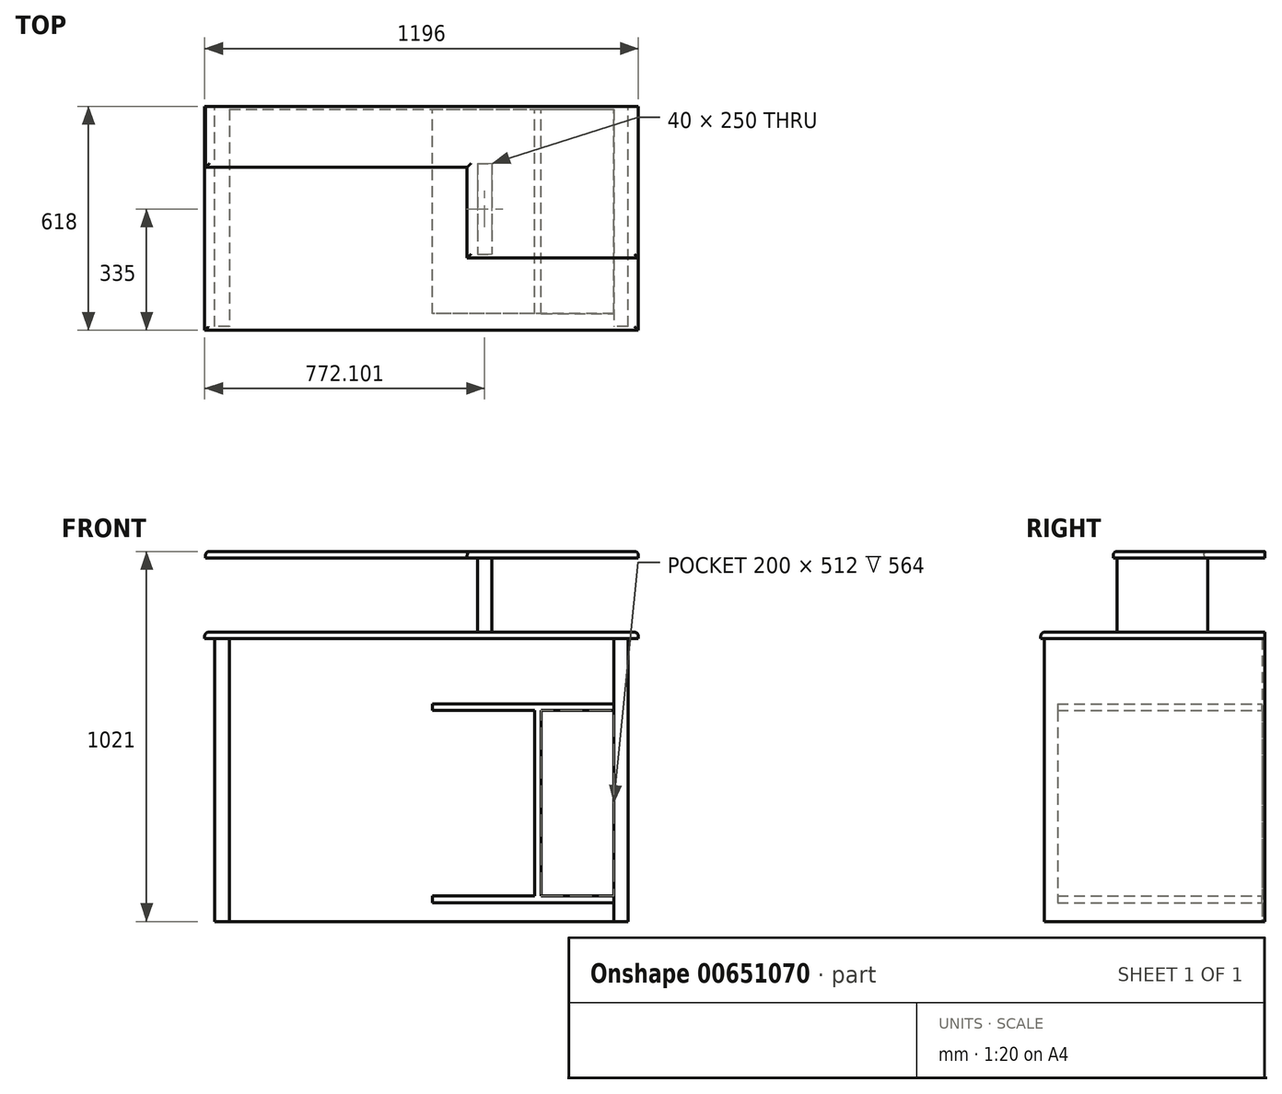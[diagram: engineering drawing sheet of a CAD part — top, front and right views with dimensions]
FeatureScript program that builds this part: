
annotation { "Feature Type Name" : "Feature", "Feature Type Description" : "" }
export const myFeature = defineFeature(function(context is Context, id is Id, definition is map)
    precondition{}
    {
        {
            var Q0;
            Q0=qCreatedBy(makeId("Top.planeOp"),FACE);
            var sketch = newSketch(context, id + "F0", { "sketchPlane" : qUnion([Q0])});
            skLineSegment(sketch, "E0.bottom", {"start": v(0, 0) * mm, "end": v(-1140, 0) * mm});
            skLineSegment(sketch, "E0.top", {"start": v(0, 608) * mm, "end": v(-1140, 608) * mm});
            skLineSegment(sketch, "E0.left", {"start": v(0, 0) * mm, "end": v(0, 608) * mm});
            skLineSegment(sketch, "E0.right", {"start": v(-1140, 0) * mm, "end": v(-1140, 608) * mm});
            skLineSegment(sketch, "E1.bottom", {"start": v(-1100, 600) * mm, "end": v(-40, 600) * mm});
            skLineSegment(sketch, "E1.top", {"start": v(-1100, 0) * mm, "end": v(-40, 0) * mm});
            skLineSegment(sketch, "E1.left", {"start": v(-1100, 600) * mm, "end": v(-1100, 0) * mm});
            skLineSegment(sketch, "E1.right", {"start": v(-40, 600) * mm, "end": v(-40, 0) * mm});
            skLineSegment(sketch, "E2.bottom", {"start": v(-558, 600) * mm, "end": v(-540, 600) * mm});
            skLineSegment(sketch, "E2.top", {"start": v(-558, 36) * mm, "end": v(-540, 36) * mm});
            skLineSegment(sketch, "E2.left", {"start": v(-558, 600) * mm, "end": v(-558, 36) * mm});
            skLineSegment(sketch, "E2.right", {"start": v(-540, 600) * mm, "end": v(-540, 36) * mm});
            skSolve(sketch);
        }
        {
            var Q0;
            Q0=makeQuery(id+"F0.imprint","IMPRINT",FACE,{"disambiguationData":[TD([[makeQuery(id+"F0.imprint","IMPRINT",EDGE,{"derivedFrom":sQuery(id+"F0.wireOp",EDGE,"E0.top")}),1.0]])]});
            var Q1;
            Q1=makeQuery(id+"F0.imprint","IMPRINT",FACE,{"disambiguationData":[TD([[makeQuery(id+"F0.imprint","IMPRINT",EDGE,{"derivedFrom":sQuery(id+"F0.wireOp",EDGE,"E2.bottom")}),-1.0]])]});
            extrude(context, id + "F1", {"entities" : qUnion([Q0, Q1]), "depth" : 780 * mm, "offsetDistance" : 25 * mm});
        }
        {
            var Q0;
            {var subQ0=sQuery(id+"F0.wireOp",EDGE,"E1.bottom");Q0=makeQuery(id+"F1.opExtrude","SWEPT_FACE",FACE,{"disambiguationData":[OSD([subQ0]),TDD([makeQuery(id+"F0.imprint","IMPRINT",EDGE,{"disambiguationData":[TD([[makeQuery(id+"F0.imprint","INTERSECT",VERTEX,{"derivedFrom":[subQ0,sQuery(id+"F0.wireOp",EDGE,"E1.right")]}),1.0]])],"derivedFrom":subQ0})])]});}
            var sketch = newSketch(context, id + "F2", { "sketchPlane" : qUnion([Q0])});
            skLineSegment(sketch, "E3.bottom", {"start": v(-540, 52) * mm, "end": v(-40, 52) * mm});
            skLineSegment(sketch, "E3.top", {"start": v(-540, 70) * mm, "end": v(-40, 70) * mm});
            skLineSegment(sketch, "E3.left", {"start": v(-540, 52) * mm, "end": v(-540, 70) * mm});
            skLineSegment(sketch, "E3.right", {"start": v(-40, 52) * mm, "end": v(-40, 70) * mm});
            skLineSegment(sketch, "E4.bottom", {"start": v(-40, 582) * mm, "end": v(-540, 582) * mm});
            skLineSegment(sketch, "E4.top", {"start": v(-40, 600) * mm, "end": v(-540, 600) * mm});
            skLineSegment(sketch, "E4.left", {"start": v(-40, 582) * mm, "end": v(-40, 600) * mm});
            skLineSegment(sketch, "E4.right", {"start": v(-540, 582) * mm, "end": v(-540, 600) * mm});
            skLineSegment(sketch, "E5.0", {"start": v(-1100, 780) * mm, "end": v(-558, 780) * mm});
            skLineSegment(sketch, "E6.bottom", {"start": v(-258, 582) * mm, "end": v(-240, 582) * mm});
            skLineSegment(sketch, "E6.top", {"start": v(-258, 70) * mm, "end": v(-240, 70) * mm});
            skLineSegment(sketch, "E6.left", {"start": v(-258, 582) * mm, "end": v(-258, 70) * mm});
            skLineSegment(sketch, "E6.right", {"start": v(-240, 582) * mm, "end": v(-240, 70) * mm});
            skSolve(sketch);
        }
        {
            var Q0;
            Q0=qSketchRegion(id+"F2",true);
            extrude(context, id + "F3", {"entities" : qUnion([Q0]), "operationType" : NewBodyOperationType.ADD, "depth" : 564 * mm, "offsetDistance" : 25 * mm});
        }
        {
            var Q0;
            Q0=makeQuery(id+"F1.opExtrude","CAP_FACE",FACE,{"disambiguationData":[OSD([sQuery(id+"F0.wireOp",EDGE,"E0.bottom"),sQuery(id+"F0.wireOp",EDGE,"E0.top"),sQuery(id+"F0.wireOp",EDGE,"E0.left"),sQuery(id+"F0.wireOp",EDGE,"E0.right"),sQuery(id+"F0.wireOp",EDGE,"E1.bottom"),sQuery(id+"F0.wireOp",EDGE,"E1.left"),sQuery(id+"F0.wireOp",EDGE,"E1.right"),sQuery(id+"F0.wireOp",EDGE,"E2.top"),sQuery(id+"F0.wireOp",EDGE,"E2.left"),sQuery(id+"F0.wireOp",EDGE,"E2.right")])],"isStart":false});
            var sketch = newSketch(context, id + "F4", { "sketchPlane" : qUnion([Q0])});
            skLineSegment(sketch, "E7.0", {"start": v(0, 608) * mm, "end": v(-1140, 608) * mm});
            skLineSegment(sketch, "E8.0", {"start": v(-1140, 0) * mm, "end": v(-1140, 608) * mm});
            skLineSegment(sketch, "E9.0", {"start": v(0, 0) * mm, "end": v(0, 608) * mm});
            skLineSegment(sketch, "E10.0", {"start": v(-1100, 0) * mm, "end": v(-1140, 0) * mm});
            skLineSegment(sketch, "E11.0", {"start": v(0, 0) * mm, "end": v(-40, 0) * mm});
            skLineSegment(sketch, "E12.bottom", {"start": v(-1168, 608) * mm, "end": v(28, 608) * mm});
            skLineSegment(sketch, "E12.top", {"start": v(-1168, -10) * mm, "end": v(28, -10) * mm});
            skLineSegment(sketch, "E12.left", {"start": v(-1168, 608) * mm, "end": v(-1168, -10) * mm});
            skLineSegment(sketch, "E12.right", {"start": v(28, 608) * mm, "end": v(28, -10) * mm});
            skSolve(sketch);
        }
        {
            var Q0;
            Q0=qSketchRegion(id+"F4",true);
            extrude(context, id + "F5", {"entities" : qUnion([Q0]), "operationType" : NewBodyOperationType.ADD, "depth" : 18 * mm, "offsetDistance" : 25 * mm});
        }
        {
            var Q0;
            Q0=makeQuery(id+"F5.opExtrude","CAP_EDGE",EDGE,{"disambiguationData":[OSD([sQuery(id+"F4.wireOp",EDGE,"E12.top")])],"isStart":false});
            var Q1;
            Q1=makeQuery(id+"F5.opExtrude","CAP_EDGE",EDGE,{"disambiguationData":[OSD([sQuery(id+"F4.wireOp",EDGE,"E12.left")])],"isStart":false});
            var Q2;
            Q2=makeQuery(id+"F5.opExtrude","CAP_EDGE",EDGE,{"disambiguationData":[OSD([sQuery(id+"F4.wireOp",EDGE,"E12.right")])],"isStart":false});
            fillet(context, id + "F6", {"entities" : qUnion([Q0, Q1, Q2]), "radius" : 10 * mm, "tangentPropagation" : true, "allowEdgeOverflow" : false});
        }
        {
            var Q0;
            Q0=makeQuery(id+"F5.opExtrude","CAP_FACE",FACE,{"disambiguationData":[OSD([sQuery(id+"F4.wireOp",EDGE,"E12.bottom"),sQuery(id+"F4.wireOp",EDGE,"E12.top"),sQuery(id+"F4.wireOp",EDGE,"E12.left"),sQuery(id+"F4.wireOp",EDGE,"E12.right")])],"isStart":false});
            var sketch = newSketch(context, id + "F7", { "sketchPlane" : qUnion([Q0])});
            skLineSegment(sketch, "E13.0.0", {"start": v(0, 608) * mm, "end": v(-1158, 608) * mm});
            skLineSegment(sketch, "E13.0.1", {"start": v(-1158, 608) * mm, "end": v(-1158, 0) * mm});
            skLineSegment(sketch, "E13.0.2", {"start": v(-1158, 0) * mm, "end": v(18, 0) * mm});
            skLineSegment(sketch, "E13.0.3", {"start": v(18, 0) * mm, "end": v(18, 608) * mm});
            skLineSegment(sketch, "E14.bottom", {"start": v(-1137.47, 608) * mm, "end": v(18, 608) * mm});
            skLineSegment(sketch, "E14.top", {"start": v(-1137.47, 450) * mm, "end": v(0, 450) * mm});
            skLineSegment(sketch, "E14.left", {"start": v(-1137.47, 608) * mm, "end": v(-1137.47, 450) * mm});
            skLineSegment(sketch, "E15", {"start": v(0, 450) * mm, "end": v(0, 608) * mm});
            skLineSegment(sketch, "E16.bottom", {"start": v(-1137.47, 450) * mm, "end": v(-1100, 450) * mm});
            skLineSegment(sketch, "E16.top", {"start": v(-1137.47, 608) * mm, "end": v(-1100, 608) * mm});
            skLineSegment(sketch, "E16.left", {"start": v(-1137.47, 450) * mm, "end": v(-1137.47, 608) * mm});
            skLineSegment(sketch, "E16.right", {"start": v(-1100, 450) * mm, "end": v(-1100, 608) * mm});
            skLineSegment(sketch, "E17.bottom", {"start": v(0, 450) * mm, "end": v(-40, 450) * mm});
            skLineSegment(sketch, "E17.top", {"start": v(0, 608) * mm, "end": v(-40, 608) * mm});
            skLineSegment(sketch, "E17.right", {"start": v(-40, 450) * mm, "end": v(-40, 608) * mm});
            skPoint(sketch, "E18.oppositeSnap0", {"position": v(18, 304) * mm});
            skLineSegment(sketch, "E18.bottom", {"start": v(-40, 450) * mm, "end": v(0, 450) * mm});
            skLineSegment(sketch, "E18.left", {"start": v(-40, 450) * mm, "end": v(-40, 200) * mm});
            skLineSegment(sketch, "E18.right", {"start": v(0, 450) * mm, "end": v(0, 200) * mm});
            skLineSegment(sketch, "E19.0", {"start": v(-1100, 600) * mm, "end": v(-40, 600) * mm});
            skLineSegment(sketch, "E20.bottom", {"start": v(-415.9, 600) * mm, "end": v(-375.9, 600) * mm});
            skLineSegment(sketch, "E20.top", {"start": v(-415.9, 200) * mm, "end": v(-375.9, 200) * mm});
            skLineSegment(sketch, "E20.left", {"start": v(-415.9, 600) * mm, "end": v(-415.9, 200) * mm});
            skLineSegment(sketch, "E20.right", {"start": v(-375.9, 600) * mm, "end": v(-375.9, 200) * mm});
            skLineSegment(sketch, "E21", {"start": v(-40, 200) * mm, "end": v(0, 200) * mm});
            skPoint(sketch, "E22.orphan", {"position": v(0, 304) * mm});
            skSolve(sketch);
        }
        {
            var Q0;
            {var subQ1=sQuery(id+"F7.wireOp",EDGE,"E16.bottom");Q0=makeQuery(id+"F7.imprint","IMPRINT",FACE,{"disambiguationData":[TD([[makeQuery(id+"F7.imprint","IMPRINT",EDGE,{"derivedFrom":subQ1}),1.0]])]});}
            var Q1;
            {var subQ5=sQuery(id+"F7.wireOp",EDGE,"E20.top");Q1=makeQuery(id+"F7.imprint","IMPRINT",FACE,{"disambiguationData":[TD([[makeQuery(id+"F7.imprint","IMPRINT",EDGE,{"derivedFrom":subQ5}),1.0]])]});}
            var Q2;
            {var subQ5=sQuery(id+"F7.wireOp",EDGE,"E20.bottom");Q2=makeQuery(id+"F7.imprint","IMPRINT",FACE,{"disambiguationData":[TD([[makeQuery(id+"F7.imprint","IMPRINT",EDGE,{"derivedFrom":subQ5}),-1.0]])]});}
            var Q3;
            {var subQ1=sQuery(id+"F7.wireOp",EDGE,"E17.top");Q3=makeQuery(id+"F7.imprint","IMPRINT",FACE,{"disambiguationData":[TD([[makeQuery(id+"F7.imprint","IMPRINT",EDGE,{"derivedFrom":subQ1}),-1.0]])]});}
            var Q4;
            Q4=makeQuery(id+"F7.imprint","IMPRINT",FACE,{"disambiguationData":[TD([[makeQuery(id+"F7.imprint","IMPRINT",EDGE,{"derivedFrom":sQuery(id+"F7.wireOp",EDGE,"E18.bottom")}),-1.0]])]});
            var Q5;
            {var subQ3=sQuery(id+"F7.wireOp",EDGE,"E20.bottom");Q5=makeQuery(id+"F7.imprint","IMPRINT",FACE,{"disambiguationData":[TD([[makeQuery(id+"F7.imprint","IMPRINT",EDGE,{"derivedFrom":subQ3}),1.0]])]});}
            extrude(context, id + "F8", {"entities" : qUnion([Q0, Q1, Q2, Q3, Q4, Q5]), "operationType" : NewBodyOperationType.ADD, "depth" : 205 * mm, "offsetDistance" : 25 * mm});
        }
        {
            var Q0;
            Q0=makeQuery(id+"F8.opExtrude","CAP_FACE",FACE,{"disambiguationData":[OSD([sQuery(id+"F7.wireOp",EDGE,"E14.bottom"),sQuery(id+"F7.wireOp",EDGE,"E16.bottom"),sQuery(id+"F7.wireOp",EDGE,"E16.top"),sQuery(id+"F7.wireOp",EDGE,"E16.left"),sQuery(id+"F7.wireOp",EDGE,"E16.right"),sQuery(id+"F7.wireOp",EDGE,"E17.top"),sQuery(id+"F7.wireOp",EDGE,"E15"),sQuery(id+"F7.wireOp",EDGE,"E17.right"),sQuery(id+"F7.wireOp",EDGE,"E18.left"),sQuery(id+"F7.wireOp",EDGE,"E18.right"),sQuery(id+"F7.wireOp",EDGE,"E19.0"),sQuery(id+"F7.wireOp",EDGE,"E20.top"),sQuery(id+"F7.wireOp",EDGE,"E20.left"),sQuery(id+"F7.wireOp",EDGE,"E20.right"),sQuery(id+"F7.wireOp",EDGE,"E21")])],"isStart":false});
            var sketch = newSketch(context, id + "F9", { "sketchPlane" : qUnion([Q0])});
            skLineSegment(sketch, "E23.0", {"start": v(-1137.47, 608) * mm, "end": v(0, 608) * mm});
            skLineSegment(sketch, "E24.0", {"start": v(-1137.47, 450) * mm, "end": v(-1137.47, 608) * mm});
            skLineSegment(sketch, "E25.0", {"start": v(0, 200) * mm, "end": v(0, 608) * mm});
            skLineSegment(sketch, "E26.0", {"start": v(-1137.47, 450) * mm, "end": v(-1100, 450) * mm});
            skLineSegment(sketch, "E27.0", {"start": v(-415.9, 200) * mm, "end": v(-375.9, 200) * mm});
            skLineSegment(sketch, "E28.bottom", {"start": v(-1165.47, 608) * mm, "end": v(28, 608) * mm});
            skLineSegment(sketch, "E28.top", {"start": v(-443.9, 190) * mm, "end": v(28, 190) * mm});
            skLineSegment(sketch, "E28.left", {"start": v(-1165.47, 608) * mm, "end": v(-1165.47, 440) * mm});
            skLineSegment(sketch, "E28.right", {"start": v(28, 608) * mm, "end": v(28, 190) * mm});
            skLineSegment(sketch, "E29", {"start": v(-1165.47, 440) * mm, "end": v(-443.9, 440) * mm});
            skLineSegment(sketch, "E30", {"start": v(-443.9, 440) * mm, "end": v(-443.9, 190) * mm});
            skSolve(sketch);
        }
        {
            var Q0;
            Q0=qSketchRegion(id+"F9",true);
            extrude(context, id + "F10", {"entities" : qUnion([Q0]), "operationType" : NewBodyOperationType.ADD, "depth" : 18 * mm, "offsetDistance" : 25 * mm});
        }
        {
            var Q0;
            Q0=makeQuery(id+"F10.opExtrude","CAP_EDGE",EDGE,{"disambiguationData":[OSD([sQuery(id+"F9.wireOp",EDGE,"E28.left")])],"isStart":false});
            var Q1;
            Q1=makeQuery(id+"F10.opExtrude","CAP_EDGE",EDGE,{"disambiguationData":[OSD([sQuery(id+"F9.wireOp",EDGE,"E29")])],"isStart":false});
            var Q2;
            Q2=makeQuery(id+"F10.opExtrude","CAP_EDGE",EDGE,{"disambiguationData":[OSD([sQuery(id+"F9.wireOp",EDGE,"E30")])],"isStart":false});
            var Q3;
            Q3=makeQuery(id+"F10.opExtrude","CAP_EDGE",EDGE,{"disambiguationData":[OSD([sQuery(id+"F9.wireOp",EDGE,"E28.top")])],"isStart":false});
            var Q4;
            Q4=makeQuery(id+"F10.opExtrude","CAP_EDGE",EDGE,{"disambiguationData":[OSD([sQuery(id+"F9.wireOp",EDGE,"E28.right")])],"isStart":false});
            fillet(context, id + "F11", {"entities" : qUnion([Q0, Q1, Q2, Q3, Q4]), "radius" : 10 * mm, "tangentPropagation" : true, "allowEdgeOverflow" : false});
        }
    });
